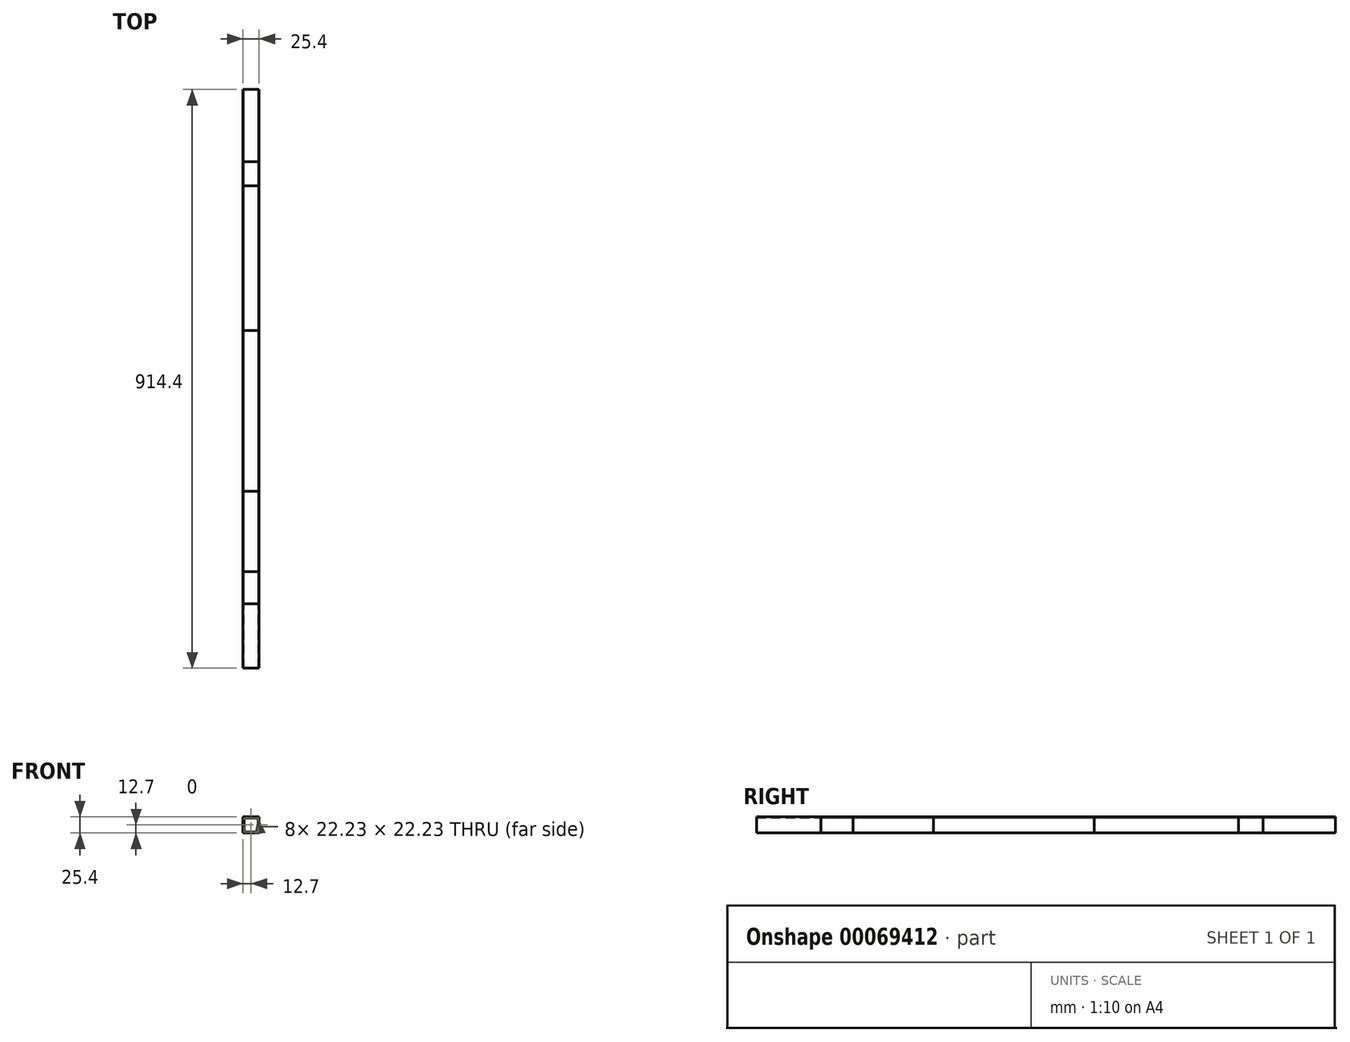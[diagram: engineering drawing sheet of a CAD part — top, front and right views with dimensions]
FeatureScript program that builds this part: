
annotation { "Feature Type Name" : "Feature", "Feature Type Description" : "" }
export const myFeature = defineFeature(function(context is Context, id is Id, definition is map)
    precondition{}
    {
        {
            var Q0;
            Q0=qCreatedBy(makeId("Front.planeOp"),FACE);
            var sketch = newSketch(context, id + "F0", { "sketchPlane" : qUnion([Q0])});
            skLineSegment(sketch, "E0.bottom", {"start": v(0, 0) * mm, "end": v(25.4, 0) * mm});
            skLineSegment(sketch, "E0.top", {"start": v(0, 25.4) * mm, "end": v(25.4, 25.4) * mm});
            skLineSegment(sketch, "E0.left", {"start": v(0, 0) * mm, "end": v(0, 25.4) * mm});
            skLineSegment(sketch, "E0.right", {"start": v(25.4, 0) * mm, "end": v(25.4, 25.4) * mm});
            skLineSegment(sketch, "E1.bottom", {"start": v(1.59, 1.59) * mm, "end": v(23.81, 1.59) * mm});
            skLineSegment(sketch, "E1.top", {"start": v(1.59, 23.81) * mm, "end": v(23.81, 23.81) * mm});
            skLineSegment(sketch, "E1.left", {"start": v(1.59, 1.59) * mm, "end": v(1.59, 23.81) * mm});
            skLineSegment(sketch, "E1.right", {"start": v(23.81, 1.59) * mm, "end": v(23.81, 23.81) * mm});
            skSolve(sketch);
        }
        {
            var Q0;
            Q0=makeQuery(id+"F0.imprint","IMPRINT",FACE,{"disambiguationData":[TD([[makeQuery(id+"F0.imprint","IMPRINT",EDGE,{"derivedFrom":sQuery(id+"F0.wireOp",EDGE,"E0.bottom")}),1.0]])]});
            extrude(context, id + "F1", {"entities" : qUnion([Q0]), "depth" : 914.4 * mm});
        }
        {
            var Q0;
            Q0 = qSketchRegion(id + "F0", true);
            extrude(context, id + "F2", {"entities" : qUnion([Q0]), "depth" : 152.4 * mm});
        }
        {
            var Q0;
            Q0 = qSketchRegion(id + "F0", true);
            extrude(context, id + "F3", {"entities" : qUnion([Q0]), "depth" : 381 * mm});
        }
        {
            var Q0;
            Q0 = qSketchRegion(id + "F0", true);
            extrude(context, id + "F4", {"entities" : qUnion([Q0]), "depth" : 381 * mm});
        }
        {
            var Q0;
            Q0 = qSketchRegion(id + "F0", true);
            extrude(context, id + "F5", {"entities" : qUnion([Q0]), "depth" : 635 * mm});
        }
        {
            var Q0;
            Q0 = qSketchRegion(id + "F0", true);
            extrude(context, id + "F6", {"entities" : qUnion([Q0]), "depth" : 812.8 * mm});
        }
        {
            var Q0;
            Q0 = qSketchRegion(id + "F0", true);
            extrude(context, id + "F7", {"entities" : qUnion([Q0]), "depth" : 114.3 * mm});
        }
        {
            var Q0;
            Q0 = qSketchRegion(id + "F0", true);
            extrude(context, id + "F8", {"entities" : qUnion([Q0]), "depth" : 762 * mm});
        }
    });
